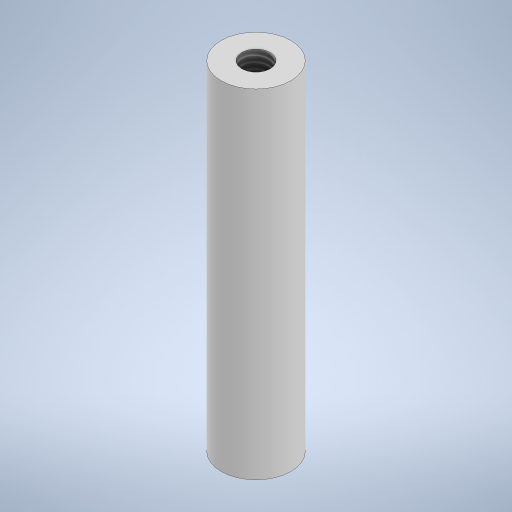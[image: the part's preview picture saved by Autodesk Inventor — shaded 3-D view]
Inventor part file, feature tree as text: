
AUTODESK INVENTOR PART (.ipt)
format: ipt  version: 2023 (Build 270158000, 158)  size: 241,664 bytes
history: native  units: in
note: dims shown in document units (in); Inventor stores cm internally (conversion verified against a paired STEP export)
features: extrude x3, sketch x3, thread x2
ambient origin geometry x8: Origin, YZ Plane, XZ Plane, XY Plane, X Axis, Y Axis, Z Axis, Center Point
bodies: Solid1 (feature_tree)
feature tree (8):
  extrude  "Extrusion1"  Depth=1.175in TaperAngle=0.0deg
  extrude  "Extrusion2"  Depth=0.38in TaperAngle=0.0deg
  thread  "Thread2"  [1 undecoded]
  extrude  "Extrusion3"  Depth=0.38in TaperAngle=0.0deg
  thread  "Thread3"  [1 undecoded]
  sketch  "Sketch1"  dims[d0=0.242in d2=1.175in d3=0.0in]
  sketch  "Sketch2"  dims[d6=0.099in d7=0.38in d8=0.0in d9=3.5in d10=0.0in]
  sketch  "Sketch3"  dims[d11=0.099in d12=0.38in d13=0.0in d14=3.5in d15=0.0in]
note: 2 required parameter values undecoded (feature->parameter linkage not recoverable at this tier; creation-order binding heuristic only, values carry confidence <= 0.55)
